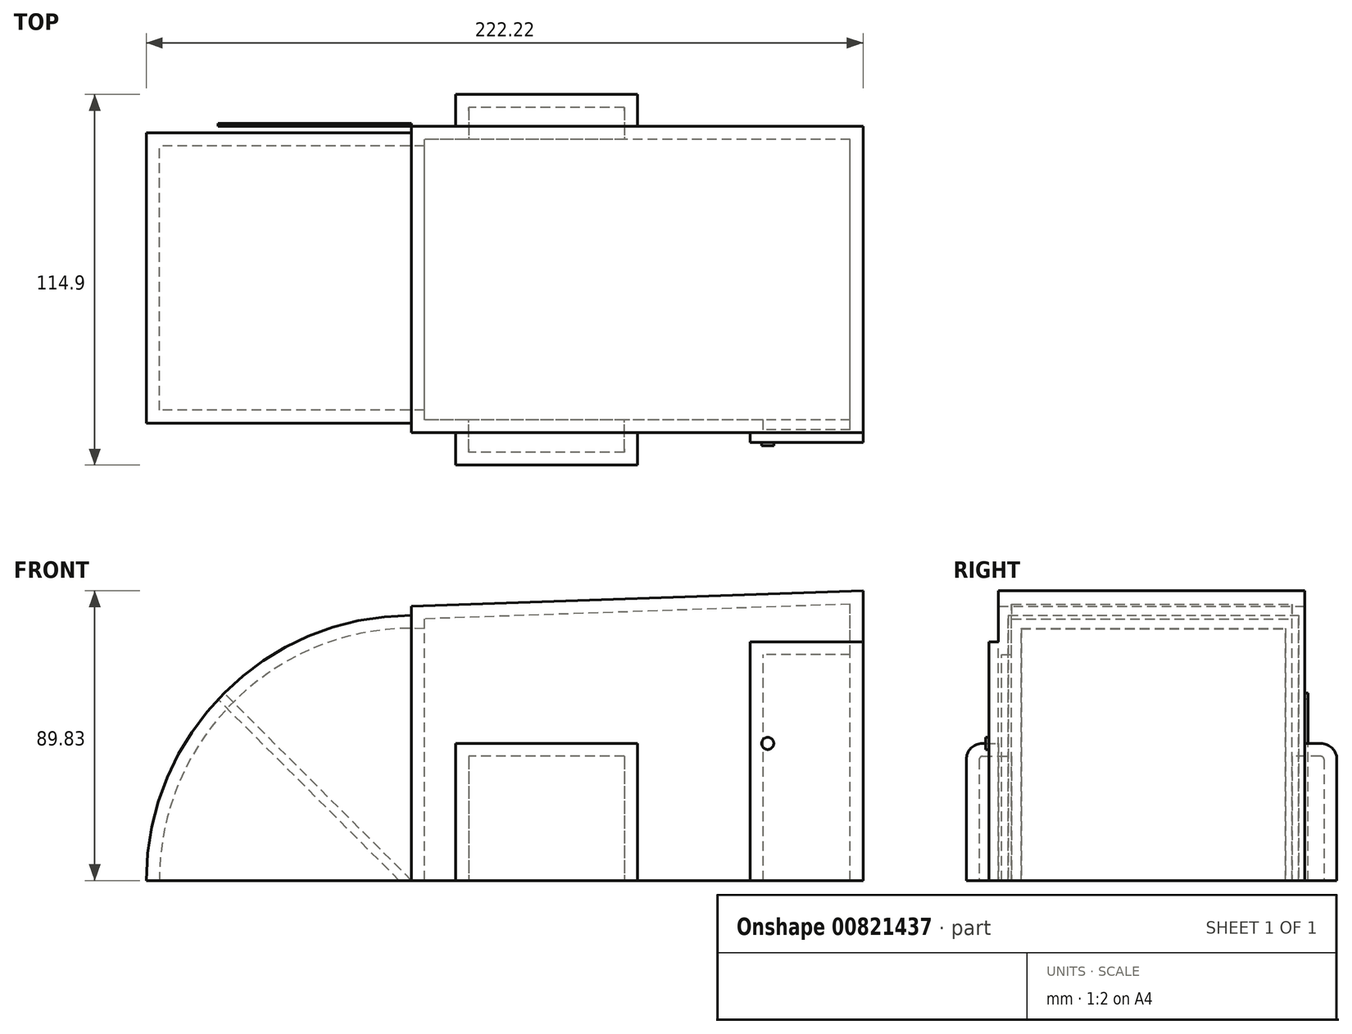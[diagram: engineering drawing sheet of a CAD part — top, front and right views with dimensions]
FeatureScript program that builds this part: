
annotation { "Feature Type Name" : "Feature", "Feature Type Description" : "" }
export const myFeature = defineFeature(function(context is Context, id is Id, definition is map)
    precondition{}
    {
        {
            var Q0;
            Q0=qCreatedBy(makeId("Front.planeOp"),FACE);
            var sketch = newSketch(context, id + "F0", { "sketchPlane" : qUnion([Q0])});
            skLineSegment(sketch, "E0.bottom", {"start": v(70, -42.5) * mm, "end": v(-70, -42.5) * mm});
            skLineSegment(sketch, "E0.right", {"start": v(-70, -42.5) * mm, "end": v(-70, 42.5) * mm});
            skPoint(sketch, "E0.middle", {"position": v(0, 0) * mm});
            skLineSegment(sketch, "E1", {"start": v(-70, -42.5) * mm, "end": v(-152.22, -42.5) * mm, "construction": true});
            skArc(sketch, "E2.trimOffspring", {"start": v(-70, 39.72) * mm, "mid": v(-128.14, 15.64) * mm, "end": v(-152.22, -42.5) * mm});
            skLineSegment(sketch, "E3", {"start": v(-70, -42.5) * mm, "end": v(-152.22, -42.5) * mm});
            skLineSegment(sketch, "E4", {"start": v(-70, -42.5) * mm, "end": v(-128.14, 15.64) * mm});
            skLineSegment(sketch, "E5", {"start": v(35, 46.12) * mm, "end": v(35, -42.5) * mm});
            skLineSegment(sketch, "E6", {"start": v(0, 0) * mm, "end": v(0, -42.5) * mm});
            skLineSegment(sketch, "E7", {"start": v(35, 31.52) * mm, "end": v(70, 31.52) * mm});
            skCircle(sketch, "E8", {"center": v(40.43, 0) * mm, "radius": 1.89 * mm});
            skLineSegment(sketch, "E9", {"start": v(-73.82, -42.5) * mm, "end": v(-130.02, 13.7) * mm});
            skLineSegment(sketch, "E10", {"start": v(70, -42.5) * mm, "end": v(70, 47.33) * mm});
            skLineSegment(sketch, "E11", {"start": v(70, 47.33) * mm, "end": v(-70, 42.5) * mm});
            skLineSegment(sketch, "E12", {"start": v(-70, -42.5) * mm, "end": v(-70, 39.72) * mm, "construction": true});
            skLineSegment(sketch, "E13", {"start": v(0, 0) * mm, "end": v(-56.32, 0) * mm});
            skLineSegment(sketch, "E14", {"start": v(-56.32, 0) * mm, "end": v(-56.32, -42.5) * mm});
            skLineSegment(sketch, "E15", {"start": v(-70, 42.5) * mm, "end": v(-75.04, 42.33) * mm});
            skLineSegment(sketch, "E16", {"start": v(-75.04, 42.33) * mm, "end": v(77.64, 47.59) * mm});
            skSolve(sketch);
        }
        {
            var Q0;
            {var subQ6=sQuery(id+"F0.wireOp",EDGE,"E6");Q0=makeQuery(id+"F0.imprint","IMPRINT",FACE,{"disambiguationData":[TD([[makeQuery(id+"F0.imprint","IMPRINT",EDGE,{"derivedFrom":subQ6}),1.0]])]});}
            var Q1;
            {var subQ3=sQuery(id+"F0.wireOp",EDGE,"E7");Q1=makeQuery(id+"F0.imprint","IMPRINT",FACE,{"disambiguationData":[TD([[makeQuery(id+"F0.imprint","IMPRINT",EDGE,{"derivedFrom":subQ3}),1.0]])]});}
            var Q2;
            {var subQ0=sQuery(id+"F0.wireOp",EDGE,"E7");Q2=makeQuery(id+"F0.imprint","IMPRINT",FACE,{"disambiguationData":[TD([[makeQuery(id+"F0.imprint","IMPRINT",EDGE,{"derivedFrom":subQ0}),-1.0]])]});}
            extrude(context, id + "F1", {"entities" : qUnion([Q0, Q1, Q2]), "depth" : 95 * mm, "offsetDistance" : 25 * mm});
        }
        {
            var Q0;
            {var subQ3=sQuery(id+"F0.wireOp",EDGE,"E6");Q0=makeQuery(id+"F0.imprint","IMPRINT",FACE,{"disambiguationData":[TD([[makeQuery(id+"F0.imprint","IMPRINT",EDGE,{"derivedFrom":subQ3}),-1.0]])]});}
            extrude(context, id + "F2", {"entities" : qUnion([Q0]), "operationType" : NewBodyOperationType.ADD, "depth" : 105 * mm, "offsetDistance" : 25 * mm});
        }
        {
            var Q0;
            {var subQ0=sQuery(id+"F0.wireOp",EDGE,"E7");Q0=makeQuery(id+"F0.imprint","IMPRINT",FACE,{"disambiguationData":[TD([[makeQuery(id+"F0.imprint","IMPRINT",EDGE,{"derivedFrom":subQ0}),-1.0]])]});}
            extrude(context, id + "F3", {"entities" : qUnion([Q0]), "operationType" : NewBodyOperationType.ADD, "depth" : 98 * mm, "offsetDistance" : 25 * mm});
        }
        {
            var Q0;
            {var subQ0=sQuery(id+"F0.wireOp",EDGE,"E4");Q0=makeQuery(id+"F0.imprint","IMPRINT",FACE,{"disambiguationData":[TD([[makeQuery(id+"F0.imprint","IMPRINT",EDGE,{"derivedFrom":subQ0}),-1.0]])]});}
            var Q1;
            {var subQ3=sQuery(id+"F0.wireOp",EDGE,"E9");Q1=makeQuery(id+"F0.imprint","IMPRINT",FACE,{"disambiguationData":[TD([[makeQuery(id+"F0.imprint","IMPRINT",EDGE,{"derivedFrom":subQ3}),1.0]])]});}
            extrude(context, id + "F4", {"entities" : qUnion([Q0, Q1]), "operationType" : NewBodyOperationType.REMOVE, "oppositeDirection" : true, "depth" : 2 * mm, "offsetDistance" : 25 * mm});
        }
        {
            var Q0;
            {var subQ0=sQuery(id+"F0.wireOp",EDGE,"E4");Q0=makeQuery(id+"F0.imprint","IMPRINT",FACE,{"disambiguationData":[TD([[makeQuery(id+"F0.imprint","IMPRINT",EDGE,{"derivedFrom":subQ0}),-1.0]])]});}
            var Q1;
            {var subQ3=sQuery(id+"F0.wireOp",EDGE,"E9");Q1=makeQuery(id+"F0.imprint","IMPRINT",FACE,{"disambiguationData":[TD([[makeQuery(id+"F0.imprint","IMPRINT",EDGE,{"derivedFrom":subQ3}),1.0]])]});}
            var Q2;
            {var subQ0=sQuery(id+"F0.wireOp",EDGE,"E4");Q2=makeQuery(id+"F0.imprint","IMPRINT",FACE,{"disambiguationData":[TD([[makeQuery(id+"F0.imprint","IMPRINT",EDGE,{"derivedFrom":subQ0}),1.0]])]});}
            extrude(context, id + "F5", {"entities" : qUnion([Q0, Q1, Q2]), "operationType" : NewBodyOperationType.REMOVE, "depth" : 2 * mm, "offsetDistance" : 25 * mm});
        }
        {
            var Q0;
            {var subQ3=sQuery(id+"F0.wireOp",EDGE,"E6");Q0=makeQuery(id+"F0.imprint","IMPRINT",FACE,{"disambiguationData":[TD([[makeQuery(id+"F0.imprint","IMPRINT",EDGE,{"derivedFrom":subQ3}),-1.0]])]});}
            extrude(context, id + "F6", {"entities" : qUnion([Q0]), "operationType" : NewBodyOperationType.ADD, "oppositeDirection" : true, "depth" : 9.9 * mm, "offsetDistance" : 25 * mm});
        }
        {
            var Q0;
            {var subQ0=sQuery(id+"F0.wireOp",EDGE,"E4");Q0=makeQuery(id+"F0.imprint","IMPRINT",FACE,{"disambiguationData":[TD([[makeQuery(id+"F0.imprint","IMPRINT",EDGE,{"derivedFrom":subQ0}),-1.0]])]});}
            var Q1;
            {var subQ3=sQuery(id+"F0.wireOp",EDGE,"E9");Q1=makeQuery(id+"F0.imprint","IMPRINT",FACE,{"disambiguationData":[TD([[makeQuery(id+"F0.imprint","IMPRINT",EDGE,{"derivedFrom":subQ3}),1.0]])]});}
            var Q2;
            {var subQ0=sQuery(id+"F0.wireOp",EDGE,"E4");Q2=makeQuery(id+"F0.imprint","IMPRINT",FACE,{"disambiguationData":[TD([[makeQuery(id+"F0.imprint","IMPRINT",EDGE,{"derivedFrom":subQ0}),1.0]])]});}
            extrude(context, id + "F7", {"entities" : qUnion([Q0, Q1, Q2]), "operationType" : NewBodyOperationType.ADD, "depth" : 92 * mm, "offsetDistance" : 25 * mm});
        }
        {
            var Q0;
            {var subQ0=sQuery(id+"F0.wireOp",EDGE,"E4");Q0=makeQuery(id+"F0.imprint","IMPRINT",FACE,{"disambiguationData":[TD([[makeQuery(id+"F0.imprint","IMPRINT",EDGE,{"derivedFrom":subQ0}),-1.0]])]});}
            var Q1;
            {var subQ3=sQuery(id+"F0.wireOp",EDGE,"E9");Q1=makeQuery(id+"F0.imprint","IMPRINT",FACE,{"disambiguationData":[TD([[makeQuery(id+"F0.imprint","IMPRINT",EDGE,{"derivedFrom":subQ3}),1.0]])]});}
            var Q2;
            {var subQ0=sQuery(id+"F0.wireOp",EDGE,"E4");Q2=makeQuery(id+"F0.imprint","IMPRINT",FACE,{"disambiguationData":[TD([[makeQuery(id+"F0.imprint","IMPRINT",EDGE,{"derivedFrom":subQ0}),1.0]])]});}
            extrude(context, id + "F8", {"entities" : qUnion([Q0, Q1, Q2]), "operationType" : NewBodyOperationType.REMOVE, "depth" : 2 * mm, "offsetDistance" : 25 * mm});
        }
        {
            var Q0;
            {var subQ0=sQuery(id+"F0.wireOp",EDGE,"E4");Q0=makeQuery(id+"F0.imprint","IMPRINT",FACE,{"disambiguationData":[TD([[makeQuery(id+"F0.imprint","IMPRINT",EDGE,{"derivedFrom":subQ0}),1.0]])]});}
            extrude(context, id + "F9", {"entities" : qUnion([Q0]), "oppositeDirection" : true, "depth" : 1 * mm, "offsetDistance" : 25 * mm});
        }
        {
            var Q0;
            Q0=makeQuery(id+"F9.opExtrude","CAP_FACE",FACE,{"disambiguationData":[OSD([sQuery(id+"F0.wireOp",EDGE,"E2.trimOffspring"),sQuery(id+"F0.wireOp",EDGE,"E3"),sQuery(id+"F0.wireOp",EDGE,"E4"),sQuery(id+"F0.wireOp",EDGE,"E9")])],"isStart":false});
            extrude(context, id + "F10", {"entities" : qUnion([Q0]), "oppositeDirection" : true, "depth" : 94 * mm, "offsetDistance" : 25 * mm});
        }
        {
            var Q0;
            Q0=makeQuery(id+"F2.opExtrude","CAP_EDGE",EDGE,{"disambiguationData":[OSD([sQuery(id+"F0.wireOp",EDGE,"E13")])],"isStart":false});
            var Q1;
            Q1=makeQuery(id+"F6.opExtrude","CAP_EDGE",EDGE,{"disambiguationData":[OSD([sQuery(id+"F0.wireOp",EDGE,"E13")])],"isStart":false});
            fillet(context, id + "F11", {"entities" : qUnion([Q0, Q1]), "radius" : 5 * mm, "tangentPropagation" : true, "allowEdgeOverflow" : false});
        }
        {
            var Q0;
            Q0=makeQuery(id+"F0.imprint","IMPRINT",FACE,{"disambiguationData":[TD([[makeQuery(id+"F0.imprint","IMPRINT",EDGE,{"derivedFrom":sQuery(id+"F0.wireOp",EDGE,"E8")}),1.0]])]});
            extrude(context, id + "F12", {"entities" : qUnion([Q0]), "operationType" : NewBodyOperationType.ADD, "depth" : 99 * mm, "offsetDistance" : 25 * mm});
        }
        {
            var Q0;
            {var subQ0=sQuery(id+"F0.wireOp",EDGE,"E3");var subQ1=sQuery(id+"F0.wireOp",EDGE,"E0.bottom");var subQ2=makeQuery(id+"F0.imprint","INTERSECT",VERTEX,{"derivedFrom":[subQ1,sQuery(id+"F0.wireOp",EDGE,"E5")]});Q0=makeQuery(id+"F7.boolean.opBoolean","MERGE",FACE,{"derivedFrom":[makeQuery(id+"F6.boolean.opBoolean","MERGE",FACE,{"derivedFrom":[makeQuery(id+"F3.boolean.opBoolean","MERGE",FACE,{"derivedFrom":[makeQuery(id+"F2.boolean.opBoolean","MERGE",FACE,{"derivedFrom":[makeQuery(id+"F1.opExtrude","SWEPT_FACE",FACE,{"disambiguationData":[OSD([subQ1]),TDD([makeQuery(id+"F0.imprint","IMPRINT",EDGE,{"disambiguationData":[TD([[makeQuery(id+"F0.imprint","INTERSECT",VERTEX,{"derivedFrom":[subQ1,sQuery(id+"F0.wireOp",EDGE,"E10")]}),-1.0]])],"derivedFrom":subQ1}),makeQuery(id+"F0.imprint","IMPRINT",EDGE,{"disambiguationData":[TD([[subQ2,-1.0]])],"derivedFrom":subQ1})])]}),makeQuery(id+"F1.opExtrude","SWEPT_FACE",FACE,{"disambiguationData":[OSD([subQ1]),TDD([makeQuery(id+"F0.imprint","IMPRINT",EDGE,{"disambiguationData":[TD([[makeQuery(id+"F0.imprint","INTERSECT",VERTEX,{"derivedFrom":[subQ1,sQuery(id+"F0.wireOp",EDGE,"E14")]}),-1.0]])],"derivedFrom":subQ1})])]}),makeQuery(id+"F2.opExtrude","SWEPT_FACE",FACE,{"disambiguationData":[OSD([subQ1])]})]}),makeQuery(id+"F3.opExtrude","SWEPT_FACE",FACE,{"disambiguationData":[OSD([subQ1])]})]}),makeQuery(id+"F6.opExtrude","SWEPT_FACE",FACE,{"disambiguationData":[OSD([subQ1])]})]}),makeQuery(id+"F7.opExtrude","SWEPT_FACE",FACE,{"disambiguationData":[OSD([subQ0])]})]});}
            shell(context, id + "F13", {"entities" : qUnion([Q0]), "thickness" : 4 * mm});
        }
        {
            var Q0;
            Q0=makeQuery(id+"F10.opExtrude","SWEPT_BODY",BODY,{"disambiguationData":[OSD([sQuery(id+"F0.wireOp",EDGE,"E2.trimOffspring"),sQuery(id+"F0.wireOp",EDGE,"E3"),sQuery(id+"F0.wireOp",EDGE,"E4"),sQuery(id+"F0.wireOp",EDGE,"E9")])]});
            deleteBodies(context, id + "F14", {"entities" : qUnion([Q0])});
        }
    });
